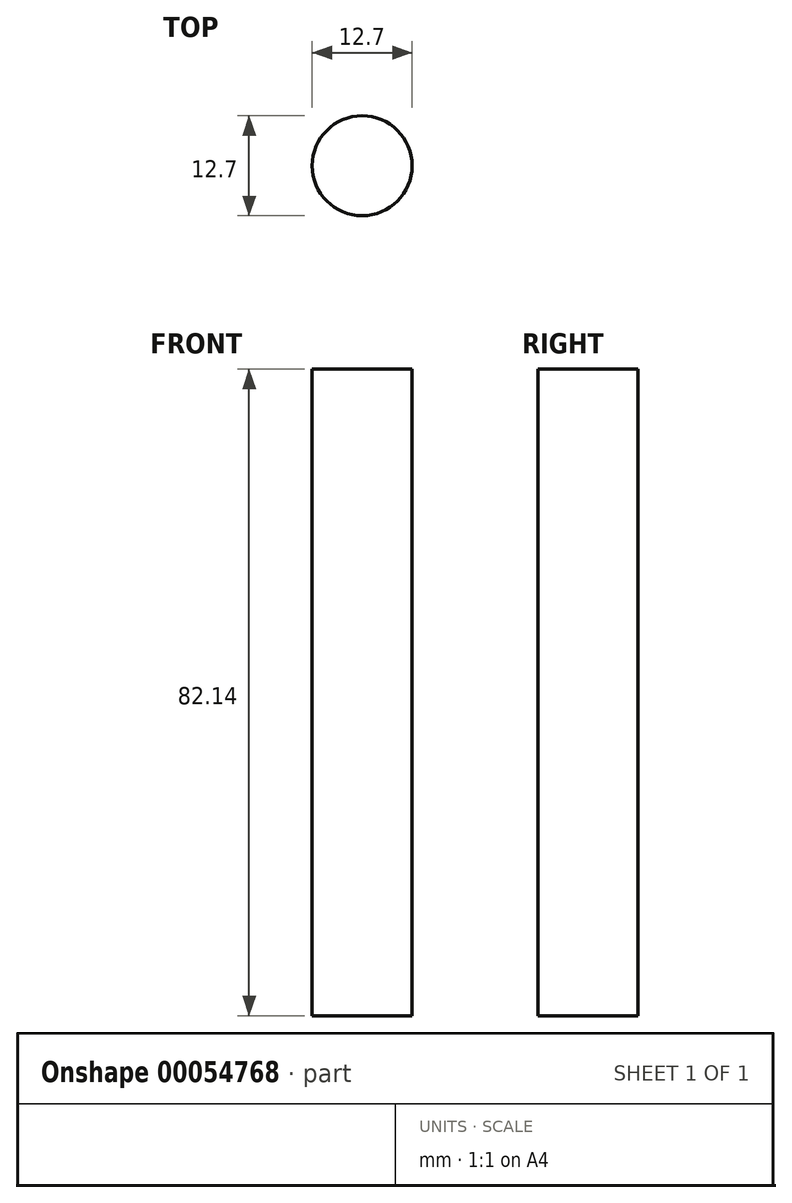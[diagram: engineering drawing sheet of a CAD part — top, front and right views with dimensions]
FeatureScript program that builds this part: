
annotation { "Feature Type Name" : "Feature", "Feature Type Description" : "" }
export const myFeature = defineFeature(function(context is Context, id is Id, definition is map)
    precondition{}
    {
        {
            var Q0;
            Q0=qCreatedBy(makeId("Top.planeOp"),FACE);
            var sketch = newSketch(context, id + "F0", { "sketchPlane" : qUnion([Q0])});
            skCircle(sketch, "E0", {"center": v(-14.67, -12.07) * mm, "radius": 6.35 * mm});
            skSolve(sketch);
        }
        {
            var Q0;
            Q0=makeQuery(id+"F0.imprint","IMPRINT",FACE,{"disambiguationData":[TD([[makeQuery(id+"F0.imprint","IMPRINT",EDGE,{"derivedFrom":sQuery(id+"F0.wireOp",EDGE,"E0")}),1.0]])]});
            extrude(context, id + "F1", {"entities" : qUnion([Q0]), "depth" : 82.14 * mm});
        }
    });
